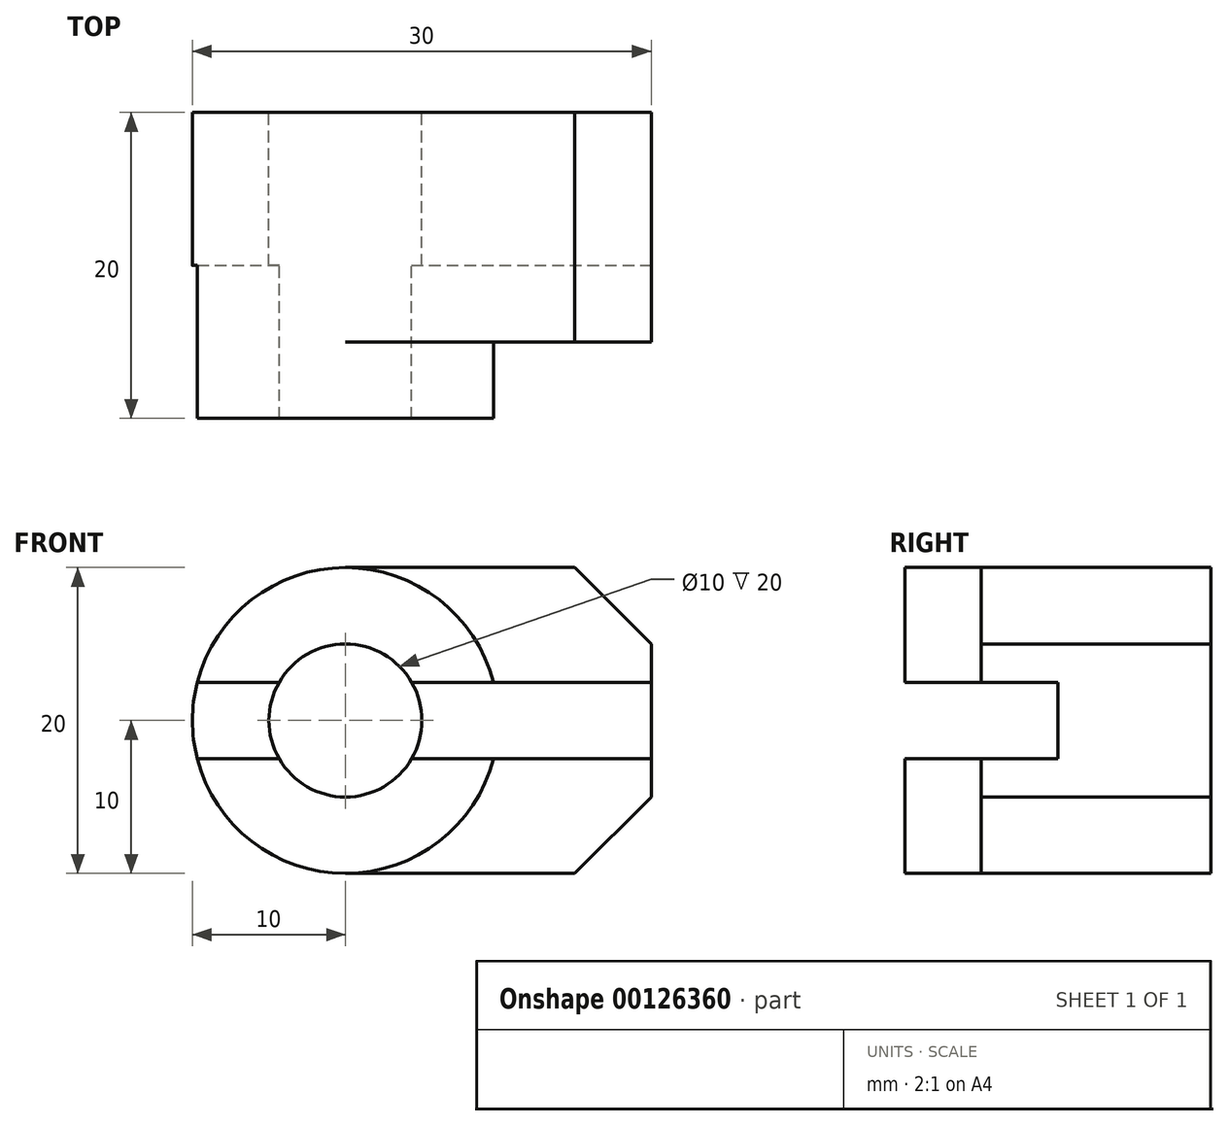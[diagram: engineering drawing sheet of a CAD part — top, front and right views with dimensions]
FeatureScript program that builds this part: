
annotation { "Feature Type Name" : "Feature", "Feature Type Description" : "" }
export const myFeature = defineFeature(function(context is Context, id is Id, definition is map)
    precondition{}
    {
        {
            var Q0;
            Q0=qCreatedBy(makeId("Front.planeOp"),FACE);
            var sketch = newSketch(context, id + "F0", { "sketchPlane" : qUnion([Q0])});
            skCircle(sketch, "E0", {"center": v(0, 0) * mm, "radius": 5 * mm});
            skCircle(sketch, "E1", {"center": v(0, 0) * mm, "radius": 10 * mm});
            skSolve(sketch);
        }
        {
            var Q0;
            Q0 = qSketchRegion(id + "F0", true);
            extrude(context, id + "F1", {"entities" : qUnion([Q0]), "depth" : 20 * mm});
        }
        {
            var Q0;
            Q0=qCreatedBy(makeId("Front.planeOp"),FACE);
            var sketch = newSketch(context, id + "F2", { "sketchPlane" : qUnion([Q0])});
            skLineSegment(sketch, "E2", {"start": v(0, 10) * mm, "end": v(15, 10) * mm});
            skLineSegment(sketch, "E3", {"start": v(15, 10) * mm, "end": v(20, 5) * mm});
            skLineSegment(sketch, "E4", {"start": v(20, 5) * mm, "end": v(20, -5) * mm});
            skLineSegment(sketch, "E5", {"start": v(20, -5) * mm, "end": v(15, -10) * mm});
            skLineSegment(sketch, "E6", {"start": v(15, -10) * mm, "end": v(0, -10) * mm});
            skCircle(sketch, "E7.0", {"center": v(0, 0) * mm, "radius": 10 * mm});
            skSolve(sketch);
        }
        {
            var Q0;
            Q0 = qSketchRegion(id + "F2", true);
            extrude(context, id + "F3", {"entities" : qUnion([Q0]), "operationType" : NewBodyOperationType.ADD, "depth" : 15 * mm});
        }
        {
            var Q0;
            Q0=makeQuery(id+"F3.boolean.opBoolean","SPLIT",FACE,{"disambiguationData":[TD([makeQuery(id+"F1.opExtrude","SWEPT_FACE",FACE,{"disambiguationData":[OSD([sQuery(id+"F0.wireOp",EDGE,"E0")])]})])],"derivedFrom":makeQuery(id+"F3.opExtrude","CAP_FACE",FACE,{"disambiguationData":[OSD([sQuery(id+"F2.wireOp",EDGE,"E2"),sQuery(id+"F2.wireOp",EDGE,"E3"),sQuery(id+"F2.wireOp",EDGE,"E4"),sQuery(id+"F2.wireOp",EDGE,"E5"),sQuery(id+"F2.wireOp",EDGE,"E6"),sQuery(id+"F2.wireOp",EDGE,"E7.0")])],"isStart":false})});
            extrude(context, id + "F4", {"entities" : qUnion([Q0]), "operationType" : NewBodyOperationType.REMOVE, "endBound" : BoundingType.THROUGH_ALL, "oppositeDirection" : true, "depth" : 25 * mm});
        }
        {
            var Q0;
            Q0=makeQuery(id+"F3.opExtrude","SWEPT_FACE",FACE,{"disambiguationData":[OSD([sQuery(id+"F2.wireOp",EDGE,"E4")])]});
            var sketch = newSketch(context, id + "F5", { "sketchPlane" : qUnion([Q0])});
            skLineSegment(sketch, "E8.bottom", {"start": v(-20, 2.5) * mm, "end": v(-10, 2.5) * mm});
            skLineSegment(sketch, "E8.top", {"start": v(-20, -2.5) * mm, "end": v(-10, -2.5) * mm});
            skLineSegment(sketch, "E8.left", {"start": v(-20, 2.5) * mm, "end": v(-20, -2.5) * mm});
            skLineSegment(sketch, "E8.right", {"start": v(-10, 2.5) * mm, "end": v(-10, -2.5) * mm});
            skLineSegment(sketch, "E9", {"start": v(-22.65, 0) * mm, "end": v(3.16, 0) * mm, "construction": true});
            skSolve(sketch);
        }
        {
            var Q0;
            Q0 = qSketchRegion(id + "F5", true);
            extrude(context, id + "F6", {"entities" : qUnion([Q0]), "operationType" : NewBodyOperationType.REMOVE, "endBound" : BoundingType.THROUGH_ALL, "oppositeDirection" : true, "depth" : 25 * mm});
        }
    });
